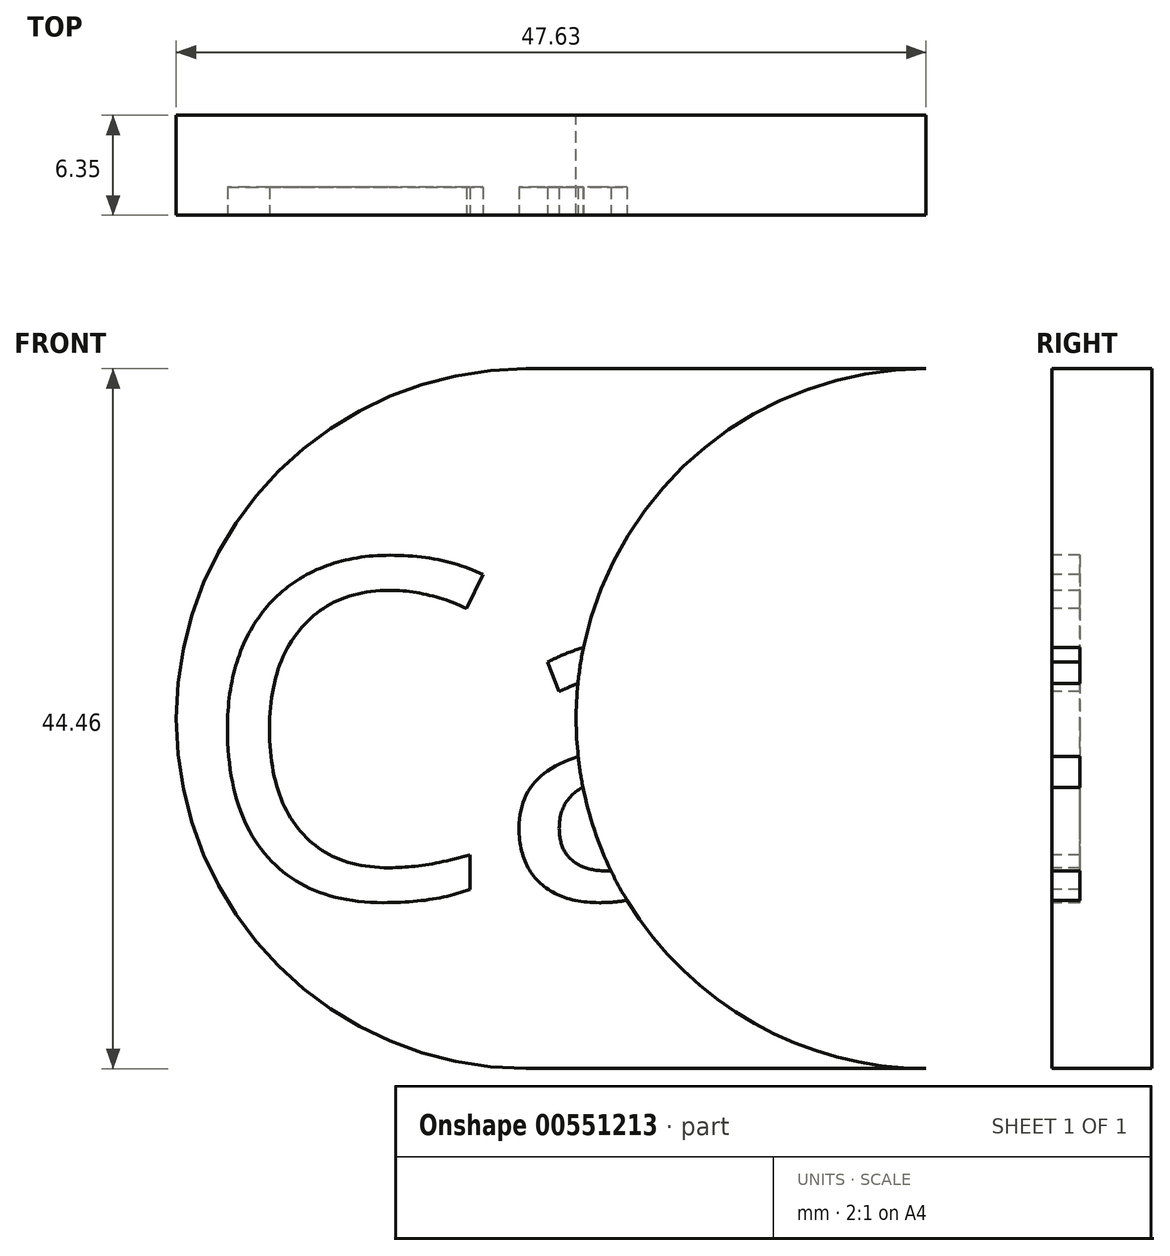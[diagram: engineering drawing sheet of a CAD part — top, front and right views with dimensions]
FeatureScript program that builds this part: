
annotation { "Feature Type Name" : "Feature", "Feature Type Description" : "" }
export const myFeature = defineFeature(function(context is Context, id is Id, definition is map)
    precondition{}
    {
        {
            var Q0;
            Q0=qCreatedBy(makeId("Front.planeOp"),FACE);
            var sketch = newSketch(context, id + "F0", { "sketchPlane" : qUnion([Q0])});
            skCircle(sketch, "E0", {"center": v(0, 0) * mm, "radius": 22.23 * mm});
            skCircle(sketch, "E1", {"center": v(25.4, 0) * mm, "radius": 22.23 * mm});
            skLineSegment(sketch, "E2", {"start": v(0, 22.22) * mm, "end": v(25.4, 22.22) * mm});
            skLineSegment(sketch, "E3", {"start": v(0, -22.23) * mm, "end": v(25.4, -22.23) * mm});
            skSolve(sketch);
        }
        {
            var Q0;
            {var subQ0=sQuery(id+"F0.wireOp",EDGE,"E1");var subQ1=sQuery(id+"F0.wireOp",EDGE,"E0");var subQ2=makeQuery(id+"F0.imprint","INTERSECT",VERTEX,{"disambiguationData":[OD(0.0)],"derivedFrom":[subQ1,subQ0]});Q0=makeQuery(id+"F0.imprint","IMPRINT",FACE,{"disambiguationData":[TD([[makeQuery(id+"F0.imprint","IMPRINT",EDGE,{"disambiguationData":[TD([[subQ2,1.0]])],"derivedFrom":subQ1}),1.0]])]});}
            var Q1;
            {var subQ0=sQuery(id+"F0.wireOp",EDGE,"E2");Q1=makeQuery(id+"F0.imprint","IMPRINT",FACE,{"disambiguationData":[TD([[makeQuery(id+"F0.imprint","IMPRINT",EDGE,{"derivedFrom":subQ0}),-1.0]])]});}
            var Q2;
            {var subQ0=sQuery(id+"F0.wireOp",EDGE,"E3");Q2=makeQuery(id+"F0.imprint","IMPRINT",FACE,{"disambiguationData":[TD([[makeQuery(id+"F0.imprint","IMPRINT",EDGE,{"derivedFrom":subQ0}),1.0]])]});}
            var Q3;
            {var subQ0=sQuery(id+"F0.wireOp",EDGE,"E0");var subQ1=makeQuery(id+"F0.imprint","INTERSECT",VERTEX,{"derivedFrom":[subQ0,sQuery(id+"F0.wireOp",EDGE,"E2")]});Q3=makeQuery(id+"F0.imprint","IMPRINT",FACE,{"disambiguationData":[TD([[makeQuery(id+"F0.imprint","IMPRINT",EDGE,{"disambiguationData":[TD([[subQ1,1.0]])],"derivedFrom":subQ0}),1.0]])]});}
            var Q4;
            {var subQ0=sQuery(id+"F0.wireOp",EDGE,"E1");var subQ1=sQuery(id+"F0.wireOp",EDGE,"E0");var subQ2=makeQuery(id+"F0.imprint","INTERSECT",VERTEX,{"disambiguationData":[OD(0.0)],"derivedFrom":[subQ1,subQ0]});Q4=makeQuery(id+"F0.imprint","IMPRINT",FACE,{"disambiguationData":[TD([[makeQuery(id+"F0.imprint","IMPRINT",EDGE,{"disambiguationData":[TD([[subQ2,1.0]])],"derivedFrom":subQ1}),-1.0]])]});}
            extrude(context, id + "F1", {"entities" : qUnion([Q0, Q1, Q2, Q3, Q4]), "depth" : 6.35 * mm});
        }
        {
            var Q0;
            Q0=makeQuery(id+"F1.opExtrude","CAP_FACE",FACE,{"disambiguationData":[OSD([sQuery(id+"F0.wireOp",EDGE,"E0"),sQuery(id+"F0.wireOp",EDGE,"E1"),sQuery(id+"F0.wireOp",EDGE,"E2"),sQuery(id+"F0.wireOp",EDGE,"E3")])],"isStart":false});
            var sketch = newSketch(context, id + "F2", { "sketchPlane" : qUnion([Q0])});
            skCircle(sketch, "E4", {"center": v(37.1, 0) * mm, "radius": 3.18 * mm});
            skSolve(sketch);
        }
        {
            var Q0;
            Q0=qSketchRegion(id+"F2",true);
            extrude(context, id + "F3", {"entities" : qUnion([Q0]), "operationType" : NewBodyOperationType.REMOVE, "oppositeDirection" : true, "depth" : 25.4 * mm});
        }
        {
            var Q0;
            Q0=makeQuery(id+"F1.opExtrude","CAP_FACE",FACE,{"disambiguationData":[OSD([sQuery(id+"F0.wireOp",EDGE,"E0"),sQuery(id+"F0.wireOp",EDGE,"E1"),sQuery(id+"F0.wireOp",EDGE,"E2"),sQuery(id+"F0.wireOp",EDGE,"E3")])],"isStart":false});
            var sketch = newSketch(context, id + "F4", { "sketchPlane" : qUnion([Q0])});
            skText(sketch, "E5", { "text": "Carl", "fontName": "OpenSans-Regular.ttf"});
            const initialGuessF4  = {"E5": [-0.02081, -0.01139, 1, 0, 0.02165]};
            skSetInitialGuess(sketch, initialGuessF4);
            skSolve(sketch);
        }
        {
            var Q0;
            Q0=qSketchRegion(id+"F4",true);
            extrude(context, id + "F5", {"entities" : qUnion([Q0]), "operationType" : NewBodyOperationType.REMOVE, "oppositeDirection" : true, "depth" : 1.78 * mm});
        }
    });
